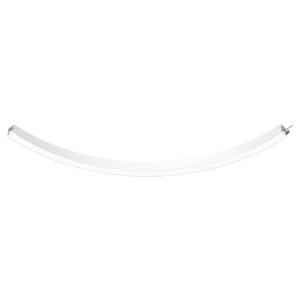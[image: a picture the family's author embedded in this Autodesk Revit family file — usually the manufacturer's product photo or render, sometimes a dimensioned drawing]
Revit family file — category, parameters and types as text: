
# Revit family: super-g_slim_super_g_slim_3000_90deg_hl_ps_led__48w_6320lm_3000k_cri_80_430-1720_00e8
name_source: partatom
category: Leuchten
revit_build: Autodesk Revit 2016 (Build: 20190508_0715(x64)
units: mm (PartAtom-declared; Revit-internal decimal feet)

## family parameters
Basisbauteil = Fläche
Beim Laden mit Abzugskörper schneiden = Nein
Bemaßung runder Anschluss = Durchmesser verwenden
Gemeinsam genutzt = Nein
Lichtquelle = Nein
Raumberechnungspunkt = Nein
Teiletyp = Normal

## types (1)
- 430-1720-D01 (1 x LED, 480 lm, 3000K)
    Approval mark = CE
    Beschreibung = The insert consists of aluminum-extruded profile. Charming SOFT-EDGE design ensure unparalleled styling. The ballast is integrated and allows for an operation with 220-240V (50/60Hz). SUPER-G SLIM (# 430-1720) ist not dimmable (on/off).
    CIE Flux Codes = 48 79 96 100 71
    Color Rendering = 1B/80…89
    Color Temperature = 3000K
    Height = 90 mm
    Hersteller = Prolicht
    Lamp Light Flux = 480 lm
    Lamp count = 1
    Lampe = 1 x LED
    Length = 147 mm
    Luminous efficacy = 103 lm/W
    ModVariant = Nein
    Modell = 430-1720
    Mounting Place = Ceiling
    Mounting Type = Pendant
    Number of Poles = 1
    OnlyDefault = Ja
    Power Factor = 1
    Product Name = SUPER-G SLIM__SUPER G SLIM 3000/90° HL PS LED: 48W 6320lm 3000K CRI:80
    Product group = Suspended profile systems
    ProductGroupID = 944
    Protection Class = Protection class I
    Protection Degree = IP 20
    RLX_Detail_Level = 1
    RlxData = <blob elided: 34217 chars, md5=df2cb5fd>
    Scheinlast = 53 VA
    Socket = socket
    Standby Power = 0 W
    System Light Flux = 5446 lm
    System Power = 53 W
    Typenbild = 430-1720.jpg
    URL = http://relux.com
    VarID = 430-1720-d01
    Voltage = 0 V
    Vorgabe-Ansicht = 1800 mm
    Weight = 0.00 kg
    Width = 65 mm

## geometry (parser evidence)
native form markers: Sweep x36
no freeform markers — native parametric forms only
